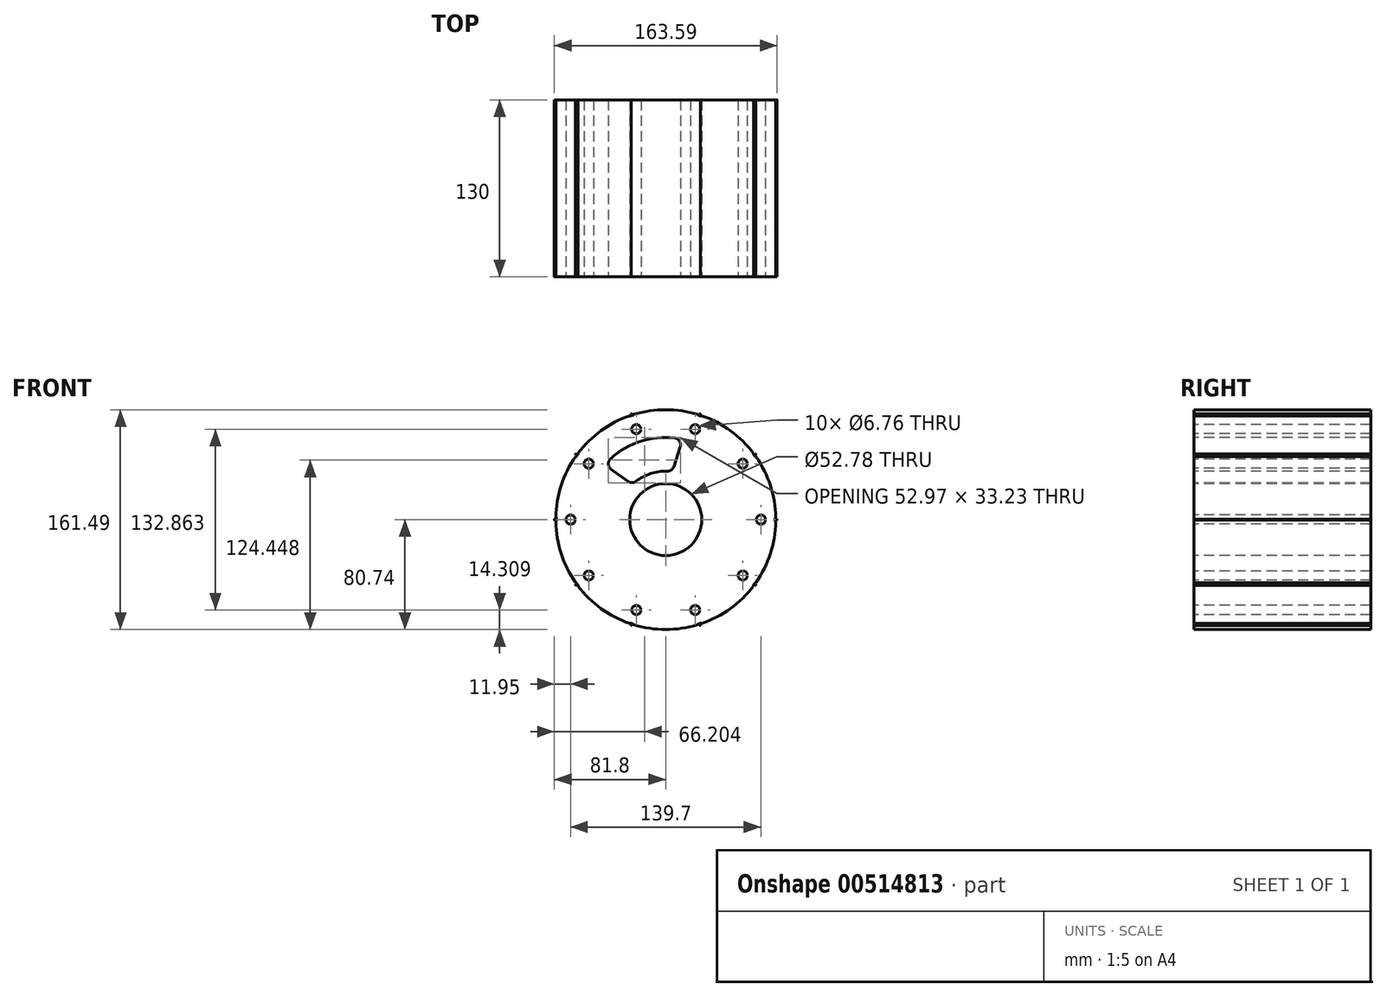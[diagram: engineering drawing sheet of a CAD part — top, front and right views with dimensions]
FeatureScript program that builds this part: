
annotation { "Feature Type Name" : "Feature", "Feature Type Description" : "" }
export const myFeature = defineFeature(function(context is Context, id is Id, definition is map)
    precondition{}
    {
        {
            var Q0;
            Q0=qCreatedBy(makeId("Front.planeOp"),FACE);
            var sketch = newSketch(context, id + "F0", { "sketchPlane" : qUnion([Q0])});
            skLineSegment(sketch, "E0", {"start": v(0, 0) * mm, "end": v(0, 59.02) * mm, "construction": true});
            skArc(sketch, "E1", {"start": v(24.79, 76.85) * mm, "mid": v(0, 80.75) * mm, "end": v(-24.79, 76.85) * mm, "construction": true});
            skArc(sketch, "E2.0", {"start": v(26, 85.9) * mm, "mid": v(0, 89.75) * mm, "end": v(-26, 85.9) * mm, "construction": true});
            skLineSegment(sketch, "E3", {"start": v(26, 85.9) * mm, "end": v(26, 80.62) * mm, "construction": true});
            skLineSegment(sketch, "E4.MirrorCS", {"start": v(-26, 80.62) * mm, "end": v(-24.79, 76.85) * mm, "construction": true});
            skLineSegment(sketch, "E5.MirrorCS", {"start": v(-26, 85.9) * mm, "end": v(-26, 80.62) * mm, "construction": true});
            skArc(sketch, "E6.1.0", {"start": v(-25.12, 76.74) * mm, "mid": v(-47.46, 65.33) * mm, "end": v(-65.22, 47.6) * mm, "construction": true});
            skArc(sketch, "E6.1.1", {"start": v(-29.46, 84.78) * mm, "mid": v(-52.75, 72.6) * mm, "end": v(-71.53, 54.21) * mm, "construction": true});
            skLineSegment(sketch, "E6.1.2", {"start": v(-71.53, 54.21) * mm, "end": v(-68.42, 49.94) * mm, "construction": true});
            skLineSegment(sketch, "E6.1.3", {"start": v(-68.42, 49.94) * mm, "end": v(-65.22, 47.6) * mm, "construction": true});
            skLineSegment(sketch, "E6.1.4", {"start": v(-29.46, 84.78) * mm, "end": v(-26.35, 80.5) * mm, "construction": true});
            skLineSegment(sketch, "E6.1.5", {"start": v(-26.35, 80.5) * mm, "end": v(-25.12, 76.74) * mm, "construction": true});
            skArc(sketch, "E6.2.0", {"start": v(-65.43, 47.32) * mm, "mid": v(-76.8, 24.95) * mm, "end": v(-80.75, 0.18) * mm, "construction": true});
            skArc(sketch, "E6.2.1", {"start": v(-73.66, 51.27) * mm, "mid": v(-85.36, 27.73) * mm, "end": v(-89.73, 1.82) * mm, "construction": true});
            skLineSegment(sketch, "E6.2.2", {"start": v(-89.73, 1.82) * mm, "end": v(-84.7, 0.18) * mm, "construction": true});
            skLineSegment(sketch, "E6.2.3", {"start": v(-84.7, 0.18) * mm, "end": v(-80.75, 0.18) * mm, "construction": true});
            skLineSegment(sketch, "E6.2.4", {"start": v(-73.66, 51.27) * mm, "end": v(-68.64, 49.64) * mm, "construction": true});
            skLineSegment(sketch, "E6.2.5", {"start": v(-68.64, 49.64) * mm, "end": v(-65.43, 47.32) * mm, "construction": true});
            skArc(sketch, "E6.3.0", {"start": v(-80.75, -0.18) * mm, "mid": v(-76.8, -24.95) * mm, "end": v(-65.43, -47.32) * mm, "construction": true});
            skArc(sketch, "E6.3.1", {"start": v(-89.73, -1.82) * mm, "mid": v(-85.36, -27.73) * mm, "end": v(-73.66, -51.27) * mm, "construction": true});
            skLineSegment(sketch, "E6.3.2", {"start": v(-73.66, -51.27) * mm, "end": v(-68.64, -49.64) * mm, "construction": true});
            skLineSegment(sketch, "E6.3.3", {"start": v(-68.64, -49.64) * mm, "end": v(-65.43, -47.32) * mm, "construction": true});
            skLineSegment(sketch, "E6.3.4", {"start": v(-89.73, -1.82) * mm, "end": v(-84.7, -0.18) * mm, "construction": true});
            skLineSegment(sketch, "E6.3.5", {"start": v(-84.7, -0.18) * mm, "end": v(-80.75, -0.18) * mm, "construction": true});
            skArc(sketch, "E6.4.0", {"start": v(-65.22, -47.6) * mm, "mid": v(-47.46, -65.33) * mm, "end": v(-25.12, -76.74) * mm, "construction": true});
            skArc(sketch, "E6.4.1", {"start": v(-71.53, -54.21) * mm, "mid": v(-52.75, -72.6) * mm, "end": v(-29.46, -84.78) * mm, "construction": true});
            skLineSegment(sketch, "E6.4.2", {"start": v(-29.46, -84.78) * mm, "end": v(-26.35, -80.5) * mm, "construction": true});
            skLineSegment(sketch, "E6.4.3", {"start": v(-26.35, -80.5) * mm, "end": v(-25.12, -76.74) * mm, "construction": true});
            skLineSegment(sketch, "E6.4.4", {"start": v(-71.53, -54.21) * mm, "end": v(-68.42, -49.94) * mm, "construction": true});
            skLineSegment(sketch, "E6.4.5", {"start": v(-68.42, -49.94) * mm, "end": v(-65.22, -47.6) * mm, "construction": true});
            skArc(sketch, "E6.5.0", {"start": v(-24.79, -76.85) * mm, "mid": v(0, -80.75) * mm, "end": v(24.79, -76.85) * mm, "construction": true});
            skArc(sketch, "E6.5.1", {"start": v(-26, -85.9) * mm, "mid": v(0, -89.75) * mm, "end": v(26, -85.9) * mm, "construction": true});
            skLineSegment(sketch, "E6.5.2", {"start": v(26, -85.9) * mm, "end": v(26, -80.62) * mm, "construction": true});
            skLineSegment(sketch, "E6.5.3", {"start": v(26, -80.62) * mm, "end": v(24.79, -76.85) * mm, "construction": true});
            skLineSegment(sketch, "E6.5.4", {"start": v(-26, -85.9) * mm, "end": v(-26, -80.62) * mm, "construction": true});
            skLineSegment(sketch, "E6.5.5", {"start": v(-26, -80.62) * mm, "end": v(-24.79, -76.85) * mm, "construction": true});
            skArc(sketch, "E6.6.0", {"start": v(25.12, -76.74) * mm, "mid": v(47.46, -65.33) * mm, "end": v(65.22, -47.6) * mm, "construction": true});
            skArc(sketch, "E6.6.1", {"start": v(29.46, -84.78) * mm, "mid": v(52.75, -72.6) * mm, "end": v(71.53, -54.21) * mm, "construction": true});
            skLineSegment(sketch, "E6.6.2", {"start": v(71.53, -54.21) * mm, "end": v(68.42, -49.94) * mm, "construction": true});
            skLineSegment(sketch, "E6.6.3", {"start": v(68.42, -49.94) * mm, "end": v(65.22, -47.6) * mm, "construction": true});
            skLineSegment(sketch, "E6.6.4", {"start": v(29.46, -84.78) * mm, "end": v(26.35, -80.5) * mm, "construction": true});
            skLineSegment(sketch, "E6.6.5", {"start": v(26.35, -80.5) * mm, "end": v(25.12, -76.74) * mm, "construction": true});
            skArc(sketch, "E6.7.0", {"start": v(65.43, -47.32) * mm, "mid": v(76.8, -24.95) * mm, "end": v(80.75, -0.18) * mm, "construction": true});
            skArc(sketch, "E6.7.1", {"start": v(73.66, -51.27) * mm, "mid": v(85.36, -27.73) * mm, "end": v(89.73, -1.82) * mm, "construction": true});
            skLineSegment(sketch, "E6.7.2", {"start": v(89.73, -1.82) * mm, "end": v(84.7, -0.18) * mm, "construction": true});
            skLineSegment(sketch, "E6.7.3", {"start": v(84.7, -0.18) * mm, "end": v(80.75, -0.18) * mm, "construction": true});
            skLineSegment(sketch, "E6.7.4", {"start": v(73.66, -51.27) * mm, "end": v(68.64, -49.64) * mm, "construction": true});
            skLineSegment(sketch, "E6.7.5", {"start": v(68.64, -49.64) * mm, "end": v(65.43, -47.32) * mm, "construction": true});
            skArc(sketch, "E6.8.0", {"start": v(80.75, 0.18) * mm, "mid": v(76.8, 24.95) * mm, "end": v(65.43, 47.32) * mm, "construction": true});
            skArc(sketch, "E6.8.1", {"start": v(89.73, 1.82) * mm, "mid": v(85.36, 27.73) * mm, "end": v(73.66, 51.27) * mm, "construction": true});
            skLineSegment(sketch, "E6.8.2", {"start": v(73.66, 51.27) * mm, "end": v(68.64, 49.64) * mm, "construction": true});
            skLineSegment(sketch, "E6.8.3", {"start": v(68.64, 49.64) * mm, "end": v(65.43, 47.32) * mm, "construction": true});
            skLineSegment(sketch, "E6.8.4", {"start": v(89.73, 1.82) * mm, "end": v(84.7, 0.18) * mm, "construction": true});
            skLineSegment(sketch, "E6.8.5", {"start": v(84.7, 0.18) * mm, "end": v(80.75, 0.18) * mm, "construction": true});
            skArc(sketch, "E6.9.0", {"start": v(65.22, 47.6) * mm, "mid": v(47.46, 65.33) * mm, "end": v(25.12, 76.74) * mm, "construction": true});
            skArc(sketch, "E6.9.1", {"start": v(71.53, 54.21) * mm, "mid": v(52.75, 72.6) * mm, "end": v(29.46, 84.78) * mm, "construction": true});
            skLineSegment(sketch, "E6.9.2", {"start": v(29.46, 84.78) * mm, "end": v(26.35, 80.5) * mm, "construction": true});
            skLineSegment(sketch, "E6.9.4", {"start": v(71.53, 54.21) * mm, "end": v(68.42, 49.94) * mm, "construction": true});
            skLineSegment(sketch, "E6.9.5", {"start": v(68.42, 49.94) * mm, "end": v(65.22, 47.6) * mm});
            skLineSegment(sketch, "E7", {"start": v(30.8, 94.8) * mm, "end": v(0, 0) * mm, "construction": true});
            skLineSegment(sketch, "E8", {"start": v(24.79, 76.85) * mm, "end": v(25.12, 76.74) * mm, "construction": true});
            skArc(sketch, "E9", {"start": v(23.36, 77.3) * mm, "mid": v(0, 80.75) * mm, "end": v(-23.36, 77.3) * mm});
            skPoint(sketch, "E10.center", {"position": v(0, -0.02) * mm});
            skPoint(sketch, "E11.visualSharp", {"position": v(23.83, 77.15) * mm});
            skPoint(sketch, "E12.newPointA", {"position": v(26.07, 76.43) * mm});
            skLineSegment(sketch, "E13.0", {"start": v(30.52, 94.9) * mm, "end": v(-0.29, 0.1) * mm, "construction": true});
            skLineSegment(sketch, "E14", {"start": v(24.67, 76.89) * mm, "end": v(24.95, 76.8) * mm, "construction": true});
            skLineSegment(sketch, "E15.0", {"start": v(24.9, 77.6) * mm, "end": v(25.18, 77.51) * mm, "construction": true});
            skLineSegment(sketch, "E16.MirrorCS", {"start": v(31.09, 94.7) * mm, "end": v(0.29, -0.1) * mm, "construction": true});
            skLineSegment(sketch, "E17.0", {"start": v(30.04, 95.04) * mm, "end": v(-0.76, 0.25) * mm, "construction": true});
            skArc(sketch, "E18.trimOffspring", {"start": v(25.47, 77.42) * mm, "mid": v(25.28, 77.8) * mm, "end": v(24.9, 77.6) * mm});
            skLineSegment(sketch, "E19", {"start": v(24.67, 76.89) * mm, "end": v(24.9, 77.6) * mm});
            skArc(sketch, "E20", {"start": v(24.67, 76.89) * mm, "mid": v(24.17, 76.54) * mm, "end": v(23.7, 76.93) * mm});
            skArc(sketch, "E21.MirrorCS", {"start": v(25.24, 76.7) * mm, "mid": v(25.43, 76.13) * mm, "end": v(26.04, 76.17) * mm});
            skPoint(sketch, "E22.newPointA", {"position": v(23.71, 77.19) * mm});
            skArc(sketch, "E22.filletArc", {"start": v(23.7, 76.93) * mm, "mid": v(23.58, 77.16) * mm, "end": v(23.36, 77.3) * mm});
            skPoint(sketch, "E23.visualSharp", {"position": v(26.19, 76.38) * mm});
            skLineSegment(sketch, "E24", {"start": v(25.24, 76.7) * mm, "end": v(25.47, 77.42) * mm});
            skArc(sketch, "E25.1.0", {"start": v(-26.53, 76.27) * mm, "mid": v(-47.46, 65.33) * mm, "end": v(-64.33, 48.8) * mm});
            skArc(sketch, "E25.1.1", {"start": v(-26.04, 76.17) * mm, "mid": v(-26.27, 76.29) * mm, "end": v(-26.53, 76.27) * mm});
            skArc(sketch, "E25.1.2", {"start": v(-25.24, 76.7) * mm, "mid": v(-25.44, 76.13) * mm, "end": v(-26.04, 76.17) * mm});
            skArc(sketch, "E25.1.3", {"start": v(-24.9, 77.6) * mm, "mid": v(-25.28, 77.8) * mm, "end": v(-25.47, 77.42) * mm});
            skLineSegment(sketch, "E25.1.4", {"start": v(-25.24, 76.7) * mm, "end": v(-25.47, 77.42) * mm});
            skLineSegment(sketch, "E25.1.5", {"start": v(-24.67, 76.9) * mm, "end": v(-24.9, 77.6) * mm});
            skArc(sketch, "E25.1.6", {"start": v(-24.67, 76.9) * mm, "mid": v(-24.17, 76.55) * mm, "end": v(-23.7, 76.93) * mm});
            skArc(sketch, "E25.2.0", {"start": v(-66.3, 46.11) * mm, "mid": v(-76.8, 24.96) * mm, "end": v(-80.73, 1.68) * mm});
            skArc(sketch, "E25.2.1", {"start": v(-65.84, 46.32) * mm, "mid": v(-66.1, 46.28) * mm, "end": v(-66.3, 46.11) * mm});
            skArc(sketch, "E25.2.2", {"start": v(-65.5, 47.23) * mm, "mid": v(-65.33, 46.65) * mm, "end": v(-65.84, 46.32) * mm});
            skArc(sketch, "E25.2.3", {"start": v(-65.76, 48.15) * mm, "mid": v(-66.18, 48.09) * mm, "end": v(-66.11, 47.67) * mm});
            skLineSegment(sketch, "E25.2.4", {"start": v(-65.5, 47.23) * mm, "end": v(-66.11, 47.67) * mm});
            skLineSegment(sketch, "E25.2.5", {"start": v(-65.15, 47.71) * mm, "end": v(-65.76, 48.15) * mm});
            skArc(sketch, "E25.2.6", {"start": v(-65.15, 47.71) * mm, "mid": v(-64.55, 47.72) * mm, "end": v(-64.4, 48.31) * mm});
            skArc(sketch, "E25.3.0", {"start": v(-80.74, -1.66) * mm, "mid": v(-76.8, -24.94) * mm, "end": v(-66.3, -46.1) * mm});
            skArc(sketch, "E25.3.1", {"start": v(-80.5, -1.22) * mm, "mid": v(-80.67, -1.4) * mm, "end": v(-80.74, -1.66) * mm});
            skArc(sketch, "E25.3.2", {"start": v(-80.75, -0.3) * mm, "mid": v(-80.27, -0.66) * mm, "end": v(-80.5, -1.22) * mm});
            skArc(sketch, "E25.3.3", {"start": v(-81.5, 0.3) * mm, "mid": v(-81.8, 0) * mm, "end": v(-81.5, -0.3) * mm});
            skLineSegment(sketch, "E25.3.4", {"start": v(-80.75, -0.3) * mm, "end": v(-81.5, -0.3) * mm});
            skLineSegment(sketch, "E25.3.5", {"start": v(-80.75, 0.3) * mm, "end": v(-81.5, 0.3) * mm});
            skArc(sketch, "E25.3.6", {"start": v(-80.75, 0.3) * mm, "mid": v(-80.27, 0.67) * mm, "end": v(-80.5, 1.24) * mm});
            skArc(sketch, "E25.4.0", {"start": v(-64.34, -48.8) * mm, "mid": v(-47.47, -65.32) * mm, "end": v(-26.54, -76.26) * mm});
            skArc(sketch, "E25.4.1", {"start": v(-64.4, -48.3) * mm, "mid": v(-64.44, -48.55) * mm, "end": v(-64.34, -48.8) * mm});
            skArc(sketch, "E25.4.2", {"start": v(-65.16, -47.7) * mm, "mid": v(-64.55, -47.7) * mm, "end": v(-64.4, -48.3) * mm});
            skArc(sketch, "E25.4.3", {"start": v(-66.12, -47.65) * mm, "mid": v(-66.19, -48.07) * mm, "end": v(-65.77, -48.14) * mm});
            skLineSegment(sketch, "E25.4.4", {"start": v(-65.16, -47.7) * mm, "end": v(-65.77, -48.14) * mm});
            skLineSegment(sketch, "E25.4.5", {"start": v(-65.51, -47.21) * mm, "end": v(-66.12, -47.65) * mm});
            skArc(sketch, "E25.4.6", {"start": v(-65.51, -47.21) * mm, "mid": v(-65.33, -46.63) * mm, "end": v(-65.85, -46.3) * mm});
            skArc(sketch, "E25.5.0", {"start": v(-23.37, -77.3) * mm, "mid": v(-0.01, -80.74) * mm, "end": v(23.35, -77.3) * mm});
            skArc(sketch, "E25.5.1", {"start": v(-23.72, -76.92) * mm, "mid": v(-23.6, -77.15) * mm, "end": v(-23.37, -77.3) * mm});
            skArc(sketch, "E25.5.2", {"start": v(-24.68, -76.88) * mm, "mid": v(-24.18, -76.54) * mm, "end": v(-23.72, -76.92) * mm});
            skArc(sketch, "E25.5.3", {"start": v(-25.48, -77.41) * mm, "mid": v(-25.29, -77.79) * mm, "end": v(-24.91, -77.6) * mm});
            skLineSegment(sketch, "E25.5.4", {"start": v(-24.68, -76.88) * mm, "end": v(-24.91, -77.6) * mm});
            skLineSegment(sketch, "E25.5.5", {"start": v(-25.25, -76.7) * mm, "end": v(-25.48, -77.41) * mm});
            skArc(sketch, "E25.5.6", {"start": v(-25.25, -76.7) * mm, "mid": v(-25.45, -76.12) * mm, "end": v(-26.05, -76.16) * mm});
            skArc(sketch, "E25.6.0", {"start": v(26.52, -76.26) * mm, "mid": v(47.45, -65.33) * mm, "end": v(64.32, -48.8) * mm});
            skArc(sketch, "E25.6.1", {"start": v(26.03, -76.17) * mm, "mid": v(26.26, -76.28) * mm, "end": v(26.52, -76.26) * mm});
            skArc(sketch, "E25.6.2", {"start": v(25.23, -76.7) * mm, "mid": v(25.42, -76.13) * mm, "end": v(26.03, -76.17) * mm});
            skArc(sketch, "E25.6.3", {"start": v(24.89, -77.6) * mm, "mid": v(25.26, -77.8) * mm, "end": v(25.46, -77.42) * mm});
            skLineSegment(sketch, "E25.6.4", {"start": v(25.23, -76.7) * mm, "end": v(25.46, -77.42) * mm});
            skLineSegment(sketch, "E25.6.5", {"start": v(24.66, -76.89) * mm, "end": v(24.89, -77.6) * mm});
            skArc(sketch, "E25.6.6", {"start": v(24.66, -76.89) * mm, "mid": v(24.16, -76.54) * mm, "end": v(23.7, -76.93) * mm});
            skArc(sketch, "E25.7.0", {"start": v(66.28, -46.1) * mm, "mid": v(76.79, -24.95) * mm, "end": v(80.72, -1.67) * mm});
            skArc(sketch, "E25.7.1", {"start": v(65.83, -46.32) * mm, "mid": v(66.09, -46.27) * mm, "end": v(66.28, -46.1) * mm});
            skArc(sketch, "E25.7.2", {"start": v(65.5, -47.22) * mm, "mid": v(65.32, -46.64) * mm, "end": v(65.83, -46.32) * mm});
            skArc(sketch, "E25.7.3", {"start": v(65.75, -48.15) * mm, "mid": v(66.17, -48.08) * mm, "end": v(66.1, -47.66) * mm});
            skLineSegment(sketch, "E25.7.4", {"start": v(65.5, -47.22) * mm, "end": v(66.1, -47.66) * mm});
            skLineSegment(sketch, "E25.7.5", {"start": v(65.14, -47.7) * mm, "end": v(65.75, -48.15) * mm});
            skArc(sketch, "E25.7.6", {"start": v(65.14, -47.7) * mm, "mid": v(64.53, -47.72) * mm, "end": v(64.38, -48.3) * mm});
            skArc(sketch, "E25.8.0", {"start": v(80.73, 1.67) * mm, "mid": v(76.8, 24.95) * mm, "end": v(66.29, 46.1) * mm});
            skArc(sketch, "E25.8.1", {"start": v(80.48, 1.23) * mm, "mid": v(80.66, 1.41) * mm, "end": v(80.73, 1.67) * mm});
            skArc(sketch, "E25.8.2", {"start": v(80.74, 0.3) * mm, "mid": v(80.26, 0.66) * mm, "end": v(80.48, 1.23) * mm});
            skArc(sketch, "E25.8.3", {"start": v(81.5, -0.3) * mm, "mid": v(81.8, 0) * mm, "end": v(81.5, 0.3) * mm});
            skLineSegment(sketch, "E25.8.4", {"start": v(80.74, 0.3) * mm, "end": v(81.5, 0.3) * mm});
            skLineSegment(sketch, "E25.8.5", {"start": v(80.74, -0.3) * mm, "end": v(81.5, -0.3) * mm});
            skArc(sketch, "E25.8.6", {"start": v(80.74, -0.3) * mm, "mid": v(80.26, -0.67) * mm, "end": v(80.48, -1.23) * mm});
            skArc(sketch, "E25.9.0", {"start": v(64.33, 48.8) * mm, "mid": v(47.46, 65.33) * mm, "end": v(26.53, 76.26) * mm});
            skArc(sketch, "E25.9.1", {"start": v(64.4, 48.3) * mm, "mid": v(64.43, 48.56) * mm, "end": v(64.33, 48.8) * mm});
            skArc(sketch, "E25.9.2", {"start": v(65.15, 47.7) * mm, "mid": v(64.54, 47.71) * mm, "end": v(64.4, 48.3) * mm});
            skArc(sketch, "E25.9.3", {"start": v(66.1, 47.66) * mm, "mid": v(66.17, 48.08) * mm, "end": v(65.76, 48.14) * mm});
            skLineSegment(sketch, "E25.9.4", {"start": v(65.15, 47.7) * mm, "end": v(65.76, 48.14) * mm});
            skLineSegment(sketch, "E25.9.5", {"start": v(65.5, 47.22) * mm, "end": v(66.1, 47.66) * mm});
            skArc(sketch, "E25.9.6", {"start": v(65.5, 47.22) * mm, "mid": v(65.32, 46.64) * mm, "end": v(65.83, 46.31) * mm});
            skPoint(sketch, "E26.orphan", {"position": v(-23.36, 77.3) * mm});
            skPoint(sketch, "E27.orphan", {"position": v(-23.7, 76.93) * mm});
            skArc(sketch, "E28.filletArc", {"start": v(-23.36, 77.3) * mm, "mid": v(-23.58, 77.16) * mm, "end": v(-23.7, 76.93) * mm});
            skPoint(sketch, "E29.newPointA", {"position": v(26.53, 76.26) * mm});
            skArc(sketch, "E29.filletArc", {"start": v(26.53, 76.26) * mm, "mid": v(26.27, 76.28) * mm, "end": v(26.04, 76.17) * mm});
            skPoint(sketch, "E30.orphan", {"position": v(-64.4, 48.3) * mm});
            skPoint(sketch, "E31.newPointB", {"position": v(-64.33, 48.8) * mm});
            skArc(sketch, "E31.filletArc", {"start": v(-64.33, 48.8) * mm, "mid": v(-64.43, 48.57) * mm, "end": v(-64.4, 48.31) * mm});
            skPoint(sketch, "E32.newPointB", {"position": v(-80.73, 1.68) * mm});
            skArc(sketch, "E32.filletArc", {"start": v(-80.73, 1.68) * mm, "mid": v(-80.67, 1.42) * mm, "end": v(-80.5, 1.24) * mm});
            skPoint(sketch, "E33.orphan", {"position": v(-65.84, -46.3) * mm});
            skPoint(sketch, "E34.newPointB", {"position": v(-66.3, -46.1) * mm});
            skArc(sketch, "E34.filletArc", {"start": v(-66.3, -46.1) * mm, "mid": v(-66.1, -46.26) * mm, "end": v(-65.85, -46.3) * mm});
            skPoint(sketch, "E35.orphan", {"position": v(-26.05, -76.16) * mm});
            skPoint(sketch, "E36.newPointB", {"position": v(-26.54, -76.26) * mm});
            skArc(sketch, "E36.filletArc", {"start": v(-26.54, -76.26) * mm, "mid": v(-26.28, -76.28) * mm, "end": v(-26.05, -76.16) * mm});
            skPoint(sketch, "E37.orphan", {"position": v(23.7, -76.92) * mm});
            skPoint(sketch, "E38.orphan", {"position": v(23.35, -77.3) * mm});
            skArc(sketch, "E39.filletArc", {"start": v(23.35, -77.3) * mm, "mid": v(23.57, -77.15) * mm, "end": v(23.7, -76.93) * mm});
            skPoint(sketch, "E40.orphan", {"position": v(64.38, -48.3) * mm});
            skPoint(sketch, "E41.orphan", {"position": v(64.32, -48.8) * mm});
            skArc(sketch, "E42.filletArc", {"start": v(64.32, -48.8) * mm, "mid": v(64.42, -48.56) * mm, "end": v(64.38, -48.3) * mm});
            skPoint(sketch, "E43.orphan", {"position": v(80.48, -1.23) * mm});
            skPoint(sketch, "E44.orphan", {"position": v(80.72, -1.67) * mm});
            skArc(sketch, "E45.filletArc", {"start": v(80.72, -1.67) * mm, "mid": v(80.66, -1.42) * mm, "end": v(80.48, -1.23) * mm});
            skPoint(sketch, "E46.orphan", {"position": v(65.83, 46.31) * mm});
            skPoint(sketch, "E47.orphan", {"position": v(66.29, 46.1) * mm});
            skArc(sketch, "E48.filletArc", {"start": v(66.29, 46.1) * mm, "mid": v(66.09, 46.27) * mm, "end": v(65.83, 46.31) * mm});
            skSolve(sketch);
        }
        {
            var Q0;
            Q0=makeQuery(id+"F0.imprint","IMPRINT",FACE,{"disambiguationData":[TD([[makeQuery(id+"F0.imprint","IMPRINT",EDGE,{"derivedFrom":sQuery(id+"F0.wireOp",EDGE,"E9")}),1.0]])]});
            extrude(context, id + "F1", {"entities" : qUnion([Q0]), "depth" : 130 * mm, "offsetDistance" : 25 * mm});
        }
        {
            var Q0;
            Q0=makeQuery(id+"F1.opExtrude","CAP_FACE",FACE,{"disambiguationData":[OSD([sQuery(id+"F0.wireOp",EDGE,"XIeMiUm1-8gPW-IMIm-pASV-yaVpRZOAZYnR"),sQuery(id+"F0.wireOp",EDGE,"Sk4poHVm-89H4-eliQ-Whh3-0xE3k8sZBWA0"),sQuery(id+"F0.wireOp",EDGE,"2de26b60-bd67-48f7-ae56-3656fd8014d00.MirrorCS"),sQuery(id+"F0.wireOp",EDGE,"JlpEmMME-SZbm-Hjtr-A6sC-niC8LgatfGaJ"),sQuery(id+"F0.wireOp",EDGE,"uWWTXu6I-KKbS-N7qE-Yg7B-Mz8SJ9bkHYqV"),sQuery(id+"F0.wireOp",EDGE,"E9"),sQuery(id+"F0.wireOp",EDGE,"E10.1.0"),sQuery(id+"F0.wireOp",EDGE,"E10.1.1"),sQuery(id+"F0.wireOp",EDGE,"E10.1.2"),sQuery(id+"F0.wireOp",EDGE,"E10.1.3"),sQuery(id+"F0.wireOp",EDGE,"E10.1.4"),sQuery(id+"F0.wireOp",EDGE,"E10.1.5"),sQuery(id+"F0.wireOp",EDGE,"E10.2.0"),sQuery(id+"F0.wireOp",EDGE,"E10.2.1"),sQuery(id+"F0.wireOp",EDGE,"E10.2.2"),sQuery(id+"F0.wireOp",EDGE,"E10.2.3"),sQuery(id+"F0.wireOp",EDGE,"E10.2.4"),sQuery(id+"F0.wireOp",EDGE,"E10.2.5"),sQuery(id+"F0.wireOp",EDGE,"E10.3.0"),sQuery(id+"F0.wireOp",EDGE,"E10.3.1"),sQuery(id+"F0.wireOp",EDGE,"E10.3.2"),sQuery(id+"F0.wireOp",EDGE,"E10.3.3"),sQuery(id+"F0.wireOp",EDGE,"E10.3.4"),sQuery(id+"F0.wireOp",EDGE,"E10.3.5"),sQuery(id+"F0.wireOp",EDGE,"E10.4.0"),sQuery(id+"F0.wireOp",EDGE,"E10.4.1"),sQuery(id+"F0.wireOp",EDGE,"E10.4.2"),sQuery(id+"F0.wireOp",EDGE,"E10.4.3"),sQuery(id+"F0.wireOp",EDGE,"E10.4.4"),sQuery(id+"F0.wireOp",EDGE,"E10.4.5"),sQuery(id+"F0.wireOp",EDGE,"E10.5.0"),sQuery(id+"F0.wireOp",EDGE,"E10.5.1"),sQuery(id+"F0.wireOp",EDGE,"E10.5.2"),sQuery(id+"F0.wireOp",EDGE,"E10.5.3"),sQuery(id+"F0.wireOp",EDGE,"E10.5.4"),sQuery(id+"F0.wireOp",EDGE,"E10.5.5"),sQuery(id+"F0.wireOp",EDGE,"E10.6.0"),sQuery(id+"F0.wireOp",EDGE,"E10.6.1"),sQuery(id+"F0.wireOp",EDGE,"E10.6.2"),sQuery(id+"F0.wireOp",EDGE,"E10.6.3"),sQuery(id+"F0.wireOp",EDGE,"E10.6.4"),sQuery(id+"F0.wireOp",EDGE,"E10.6.5"),sQuery(id+"F0.wireOp",EDGE,"E10.7.0"),sQuery(id+"F0.wireOp",EDGE,"E10.7.1"),sQuery(id+"F0.wireOp",EDGE,"E10.7.2"),sQuery(id+"F0.wireOp",EDGE,"E10.7.3"),sQuery(id+"F0.wireOp",EDGE,"E10.7.4"),sQuery(id+"F0.wireOp",EDGE,"E10.7.5"),sQuery(id+"F0.wireOp",EDGE,"E10.8.0"),sQuery(id+"F0.wireOp",EDGE,"E10.8.1"),sQuery(id+"F0.wireOp",EDGE,"E10.8.2"),sQuery(id+"F0.wireOp",EDGE,"E10.8.3"),sQuery(id+"F0.wireOp",EDGE,"E10.8.4"),sQuery(id+"F0.wireOp",EDGE,"E10.8.5"),sQuery(id+"F0.wireOp",EDGE,"E10.9.0"),sQuery(id+"F0.wireOp",EDGE,"E10.9.1"),sQuery(id+"F0.wireOp",EDGE,"E10.9.2"),sQuery(id+"F0.wireOp",EDGE,"E10.9.3"),sQuery(id+"F0.wireOp",EDGE,"E10.9.4"),sQuery(id+"F0.wireOp",EDGE,"E10.9.5")])],"isStart":false});
            var sketch = newSketch(context, id + "F2", { "sketchPlane" : qUnion([Q0])});
            skLineSegment(sketch, "E49", {"start": v(22.82, 70.22) * mm, "end": v(0, 0) * mm, "construction": true});
            skLineSegment(sketch, "E50", {"start": v(0, 0) * mm, "end": v(0, 83.92) * mm, "construction": true});
            skPoint(sketch, "E51.center", {"position": v(0, 0) * mm});
            skCircle(sketch, "E52", {"center": v(0, 0) * mm, "radius": 69.85 * mm, "construction": true});
            skPoint(sketch, "E53", {"position": v(21.58, 66.43) * mm});
            skPoint(sketch, "E54.1.0", {"position": v(-21.58, 66.43) * mm});
            skPoint(sketch, "E54.2.0", {"position": v(-56.5, 41.06) * mm});
            skPoint(sketch, "E54.3.0", {"position": v(-69.85, 0) * mm});
            skPoint(sketch, "E54.4.0", {"position": v(-56.5, -41.06) * mm});
            skPoint(sketch, "E54.5.0", {"position": v(-21.58, -66.43) * mm});
            skPoint(sketch, "E54.6.0", {"position": v(21.58, -66.43) * mm});
            skPoint(sketch, "E54.7.0", {"position": v(56.5, -41.06) * mm});
            skPoint(sketch, "E54.8.0", {"position": v(69.85, 0) * mm});
            skPoint(sketch, "E54.9.0", {"position": v(56.5, 41.06) * mm});
            skCircle(sketch, "E55", {"center": v(0, 0) * mm, "radius": 26.4 * mm});
            skSolve(sketch);
        }
        {
            var Q0;
            Q0=makeQuery(id+"F2.imprint","IMPRINT",FACE,{"disambiguationData":[TD([[makeQuery(id+"F2.imprint","IMPRINT",EDGE,{"derivedFrom":sQuery(id+"F2.wireOp",EDGE,"E55")}),1.0]])]});
            extrude(context, id + "F3", {"entities" : qUnion([Q0]), "operationType" : NewBodyOperationType.REMOVE, "endBound" : BoundingType.UP_TO_NEXT, "oppositeDirection" : true, "depth" : 25 * mm, "offsetDistance" : 25 * mm});
        }
        {
            var Q0;
            Q0=sQuery(id+"F2.wireOp",VERTEX,"E53");
            var Q1;
            Q1=sQuery(id+"F2.wireOp",VERTEX,"E54.1.0");
            var Q2;
            Q2=sQuery(id+"F2.wireOp",VERTEX,"E54.2.0");
            var Q3;
            Q3=sQuery(id+"F2.wireOp",VERTEX,"E54.3.0");
            var Q4;
            Q4=sQuery(id+"F2.wireOp",VERTEX,"E54.4.0");
            var Q5;
            Q5=sQuery(id+"F2.wireOp",VERTEX,"E54.5.0");
            var Q6;
            Q6=sQuery(id+"F2.wireOp",VERTEX,"E54.6.0");
            var Q7;
            Q7=sQuery(id+"F2.wireOp",VERTEX,"E54.7.0");
            var Q8;
            Q8=sQuery(id+"F2.wireOp",VERTEX,"E54.8.0");
            var Q9;
            Q9=sQuery(id+"F2.wireOp",VERTEX,"E54.9.0");
            var Q10;
            Q10=makeQuery(id+"F1.opExtrude","SWEPT_BODY",BODY,{"disambiguationData":[OSD([sQuery(id+"F0.wireOp",EDGE,"XIeMiUm1-8gPW-IMIm-pASV-yaVpRZOAZYnR"),sQuery(id+"F0.wireOp",EDGE,"Sk4poHVm-89H4-eliQ-Whh3-0xE3k8sZBWA0"),sQuery(id+"F0.wireOp",EDGE,"2de26b60-bd67-48f7-ae56-3656fd8014d00.MirrorCS"),sQuery(id+"F0.wireOp",EDGE,"JlpEmMME-SZbm-Hjtr-A6sC-niC8LgatfGaJ"),sQuery(id+"F0.wireOp",EDGE,"uWWTXu6I-KKbS-N7qE-Yg7B-Mz8SJ9bkHYqV"),sQuery(id+"F0.wireOp",EDGE,"E9"),sQuery(id+"F0.wireOp",EDGE,"E10.1.0"),sQuery(id+"F0.wireOp",EDGE,"E10.1.1"),sQuery(id+"F0.wireOp",EDGE,"E10.1.2"),sQuery(id+"F0.wireOp",EDGE,"E10.1.3"),sQuery(id+"F0.wireOp",EDGE,"E10.1.4"),sQuery(id+"F0.wireOp",EDGE,"E10.1.5"),sQuery(id+"F0.wireOp",EDGE,"E10.2.0"),sQuery(id+"F0.wireOp",EDGE,"E10.2.1"),sQuery(id+"F0.wireOp",EDGE,"E10.2.2"),sQuery(id+"F0.wireOp",EDGE,"E10.2.3"),sQuery(id+"F0.wireOp",EDGE,"E10.2.4"),sQuery(id+"F0.wireOp",EDGE,"E10.2.5"),sQuery(id+"F0.wireOp",EDGE,"E10.3.0"),sQuery(id+"F0.wireOp",EDGE,"E10.3.1"),sQuery(id+"F0.wireOp",EDGE,"E10.3.2"),sQuery(id+"F0.wireOp",EDGE,"E10.3.3"),sQuery(id+"F0.wireOp",EDGE,"E10.3.4"),sQuery(id+"F0.wireOp",EDGE,"E10.3.5"),sQuery(id+"F0.wireOp",EDGE,"E10.4.0"),sQuery(id+"F0.wireOp",EDGE,"E10.4.1"),sQuery(id+"F0.wireOp",EDGE,"E10.4.2"),sQuery(id+"F0.wireOp",EDGE,"E10.4.3"),sQuery(id+"F0.wireOp",EDGE,"E10.4.4"),sQuery(id+"F0.wireOp",EDGE,"E10.4.5"),sQuery(id+"F0.wireOp",EDGE,"E10.5.0"),sQuery(id+"F0.wireOp",EDGE,"E10.5.1"),sQuery(id+"F0.wireOp",EDGE,"E10.5.2"),sQuery(id+"F0.wireOp",EDGE,"E10.5.3"),sQuery(id+"F0.wireOp",EDGE,"E10.5.4"),sQuery(id+"F0.wireOp",EDGE,"E10.5.5"),sQuery(id+"F0.wireOp",EDGE,"E10.6.0"),sQuery(id+"F0.wireOp",EDGE,"E10.6.1"),sQuery(id+"F0.wireOp",EDGE,"E10.6.2"),sQuery(id+"F0.wireOp",EDGE,"E10.6.3"),sQuery(id+"F0.wireOp",EDGE,"E10.6.4"),sQuery(id+"F0.wireOp",EDGE,"E10.6.5"),sQuery(id+"F0.wireOp",EDGE,"E10.7.0"),sQuery(id+"F0.wireOp",EDGE,"E10.7.1"),sQuery(id+"F0.wireOp",EDGE,"E10.7.2"),sQuery(id+"F0.wireOp",EDGE,"E10.7.3"),sQuery(id+"F0.wireOp",EDGE,"E10.7.4"),sQuery(id+"F0.wireOp",EDGE,"E10.7.5"),sQuery(id+"F0.wireOp",EDGE,"E10.8.0"),sQuery(id+"F0.wireOp",EDGE,"E10.8.1"),sQuery(id+"F0.wireOp",EDGE,"E10.8.2"),sQuery(id+"F0.wireOp",EDGE,"E10.8.3"),sQuery(id+"F0.wireOp",EDGE,"E10.8.4"),sQuery(id+"F0.wireOp",EDGE,"E10.8.5"),sQuery(id+"F0.wireOp",EDGE,"E10.9.0"),sQuery(id+"F0.wireOp",EDGE,"E10.9.1"),sQuery(id+"F0.wireOp",EDGE,"E10.9.2"),sQuery(id+"F0.wireOp",EDGE,"E10.9.3"),sQuery(id+"F0.wireOp",EDGE,"E10.9.4"),sQuery(id+"F0.wireOp",EDGE,"E10.9.5")])]});
            hole(context, id + "F4", {"style" : HoleStyle.SIMPLE, "endStyle" : HoleEndStyle.THROUGH, "standardTappedOrClearance" : lookupTablePath({ "standard" : "ANSI", "fit" : "Normal (ASME)", "size" : "1/4", "type" : "Clearance" }), "standardBlindInLast" : lookupTablePath({ "fit" : "Free", "standard" : "ANSI", "size" : "1/4", "type" : "Clearance" }), "holeDiameter" : 6.76 * mm, "tappedDepth" : 25.4 * mm, "tapClearance" : 3, "startFromSketch" : true, "locations" : qUnion([Q0, Q1, Q2, Q3, Q4, Q5, Q6, Q7, Q8, Q9]), "scope" : qUnion([Q10])});
        }
        {
            var Q0;
            Q0=makeQuery(id+"F1.opExtrude","CAP_FACE",FACE,{"disambiguationData":[OSD([sQuery(id+"F0.wireOp",EDGE,"XIeMiUm1-8gPW-IMIm-pASV-yaVpRZOAZYnR"),sQuery(id+"F0.wireOp",EDGE,"Sk4poHVm-89H4-eliQ-Whh3-0xE3k8sZBWA0"),sQuery(id+"F0.wireOp",EDGE,"2de26b60-bd67-48f7-ae56-3656fd8014d00.MirrorCS"),sQuery(id+"F0.wireOp",EDGE,"JlpEmMME-SZbm-Hjtr-A6sC-niC8LgatfGaJ"),sQuery(id+"F0.wireOp",EDGE,"uWWTXu6I-KKbS-N7qE-Yg7B-Mz8SJ9bkHYqV"),sQuery(id+"F0.wireOp",EDGE,"E9"),sQuery(id+"F0.wireOp",EDGE,"E10.1.0"),sQuery(id+"F0.wireOp",EDGE,"E10.1.1"),sQuery(id+"F0.wireOp",EDGE,"E10.1.2"),sQuery(id+"F0.wireOp",EDGE,"E10.1.3"),sQuery(id+"F0.wireOp",EDGE,"E10.1.4"),sQuery(id+"F0.wireOp",EDGE,"E10.1.5"),sQuery(id+"F0.wireOp",EDGE,"E10.2.0"),sQuery(id+"F0.wireOp",EDGE,"E10.2.1"),sQuery(id+"F0.wireOp",EDGE,"E10.2.2"),sQuery(id+"F0.wireOp",EDGE,"E10.2.3"),sQuery(id+"F0.wireOp",EDGE,"E10.2.4"),sQuery(id+"F0.wireOp",EDGE,"E10.2.5"),sQuery(id+"F0.wireOp",EDGE,"E10.3.0"),sQuery(id+"F0.wireOp",EDGE,"E10.3.1"),sQuery(id+"F0.wireOp",EDGE,"E10.3.2"),sQuery(id+"F0.wireOp",EDGE,"E10.3.3"),sQuery(id+"F0.wireOp",EDGE,"E10.3.4"),sQuery(id+"F0.wireOp",EDGE,"E10.3.5"),sQuery(id+"F0.wireOp",EDGE,"E10.4.0"),sQuery(id+"F0.wireOp",EDGE,"E10.4.1"),sQuery(id+"F0.wireOp",EDGE,"E10.4.2"),sQuery(id+"F0.wireOp",EDGE,"E10.4.3"),sQuery(id+"F0.wireOp",EDGE,"E10.4.4"),sQuery(id+"F0.wireOp",EDGE,"E10.4.5"),sQuery(id+"F0.wireOp",EDGE,"E10.5.0"),sQuery(id+"F0.wireOp",EDGE,"E10.5.1"),sQuery(id+"F0.wireOp",EDGE,"E10.5.2"),sQuery(id+"F0.wireOp",EDGE,"E10.5.3"),sQuery(id+"F0.wireOp",EDGE,"E10.5.4"),sQuery(id+"F0.wireOp",EDGE,"E10.5.5"),sQuery(id+"F0.wireOp",EDGE,"E10.6.0"),sQuery(id+"F0.wireOp",EDGE,"E10.6.1"),sQuery(id+"F0.wireOp",EDGE,"E10.6.2"),sQuery(id+"F0.wireOp",EDGE,"E10.6.3"),sQuery(id+"F0.wireOp",EDGE,"E10.6.4"),sQuery(id+"F0.wireOp",EDGE,"E10.6.5"),sQuery(id+"F0.wireOp",EDGE,"E10.7.0"),sQuery(id+"F0.wireOp",EDGE,"E10.7.1"),sQuery(id+"F0.wireOp",EDGE,"E10.7.2"),sQuery(id+"F0.wireOp",EDGE,"E10.7.3"),sQuery(id+"F0.wireOp",EDGE,"E10.7.4"),sQuery(id+"F0.wireOp",EDGE,"E10.7.5"),sQuery(id+"F0.wireOp",EDGE,"E10.8.0"),sQuery(id+"F0.wireOp",EDGE,"E10.8.1"),sQuery(id+"F0.wireOp",EDGE,"E10.8.2"),sQuery(id+"F0.wireOp",EDGE,"E10.8.3"),sQuery(id+"F0.wireOp",EDGE,"E10.8.4"),sQuery(id+"F0.wireOp",EDGE,"E10.8.5"),sQuery(id+"F0.wireOp",EDGE,"E10.9.0"),sQuery(id+"F0.wireOp",EDGE,"E10.9.1"),sQuery(id+"F0.wireOp",EDGE,"E10.9.2"),sQuery(id+"F0.wireOp",EDGE,"E10.9.3"),sQuery(id+"F0.wireOp",EDGE,"E10.9.4"),sQuery(id+"F0.wireOp",EDGE,"E10.9.5")])],"isStart":false});
            var sketch = newSketch(context, id + "F5", { "sketchPlane" : qUnion([Q0])});
            skLineSegment(sketch, "E56", {"start": v(0, 0) * mm, "end": v(21.58, 66.43) * mm, "construction": true});
            skLineSegment(sketch, "E57", {"start": v(-56.5, 41.06) * mm, "end": v(0, 0) * mm, "construction": true});
            skLineSegment(sketch, "E58.0", {"start": v(-44.8, 40.4) * mm, "end": v(-24.57, 25.7) * mm});
            skCircle(sketch, "E59", {"center": v(0, 0) * mm, "radius": 60.33 * mm, "construction": true});
            skCircle(sketch, "E60", {"center": v(0, 0) * mm, "radius": 35.56 * mm, "construction": true});
            skArc(sketch, "E61", {"start": v(12.5, 59.02) * mm, "mid": v(-18.64, 57.37) * mm, "end": v(-44.8, 40.4) * mm});
            skArc(sketch, "E62", {"start": v(4.77, 35.24) * mm, "mid": v(-10.99, 33.82) * mm, "end": v(-24.57, 25.7) * mm});
            skLineSegment(sketch, "E63.trimOffspring", {"start": v(4.77, 35.24) * mm, "end": v(12.5, 59.02) * mm});
            skSolve(sketch);
        }
        {
            var Q0;
            Q0=qSketchRegion(id+"F5",true);
            extrude(context, id + "F6", {"entities" : qUnion([Q0]), "operationType" : NewBodyOperationType.REMOVE, "endBound" : BoundingType.UP_TO_NEXT, "oppositeDirection" : true, "depth" : 25 * mm, "offsetDistance" : 25 * mm});
        }
        {
            var Q0;
            Q0=makeQuery(id+"F6.boolean.opBoolean","COPY",EDGE,{"derivedFrom":makeQuery(id+"F6.opExtrude","SWEPT_EDGE",EDGE,{"disambiguationData":[OSD([sQuery(id+"F5.wireOp",EDGE,"E58.0"),sQuery(id+"F5.wireOp",EDGE,"E61")])]})});
            var Q1;
            Q1=makeQuery(id+"F6.boolean.opBoolean","COPY",EDGE,{"derivedFrom":makeQuery(id+"F6.opExtrude","SWEPT_EDGE",EDGE,{"disambiguationData":[OSD([sQuery(id+"F5.wireOp",EDGE,"E58.0"),sQuery(id+"F5.wireOp",EDGE,"E62")])]})});
            var Q2;
            Q2=makeQuery(id+"F6.boolean.opBoolean","COPY",EDGE,{"derivedFrom":makeQuery(id+"F6.opExtrude","SWEPT_EDGE",EDGE,{"disambiguationData":[OSD([sQuery(id+"F5.wireOp",EDGE,"E62"),sQuery(id+"F5.wireOp",EDGE,"E63.trimOffspring")])]})});
            var Q3;
            Q3=makeQuery(id+"F6.boolean.opBoolean","COPY",EDGE,{"derivedFrom":makeQuery(id+"F6.opExtrude","SWEPT_EDGE",EDGE,{"disambiguationData":[OSD([sQuery(id+"F5.wireOp",EDGE,"E61"),sQuery(id+"F5.wireOp",EDGE,"E63.trimOffspring")])]})});
            fillet(context, id + "F7", {"entities" : qUnion([Q0, Q1, Q2, Q3]), "radius" : 5.08 * mm, "tangentPropagation" : true, "allowEdgeOverflow" : false});
        }
    });
